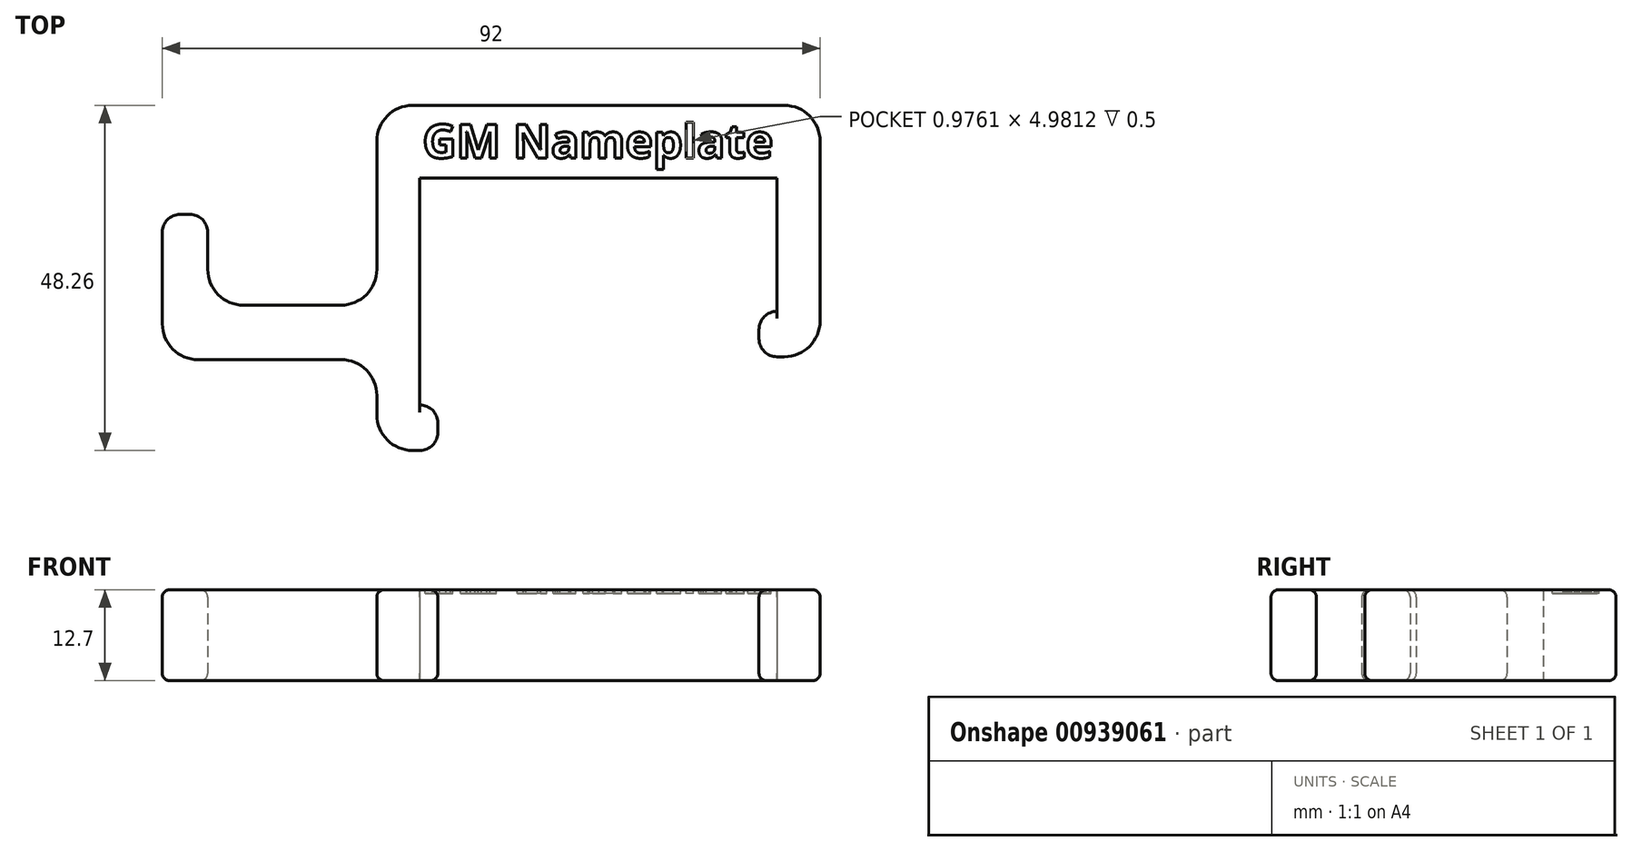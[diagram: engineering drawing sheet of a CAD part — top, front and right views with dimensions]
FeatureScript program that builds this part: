
annotation { "Feature Type Name" : "Feature", "Feature Type Description" : "" }
export const myFeature = defineFeature(function(context is Context, id is Id, definition is map)
    precondition{}
    {
        {
            var Q0;
            Q0=qCreatedBy(makeId("Top.planeOp"),FACE);
            var sketch = newSketch(context, id + "F0", { "sketchPlane" : qUnion([Q0])});
            skLineSegment(sketch, "E0.bottom", {"start": v(-25, 0) * mm, "end": v(25, 0) * mm});
            skLineSegment(sketch, "E0.top", {"start": v(-25, -10.16) * mm, "end": v(25, -10.16) * mm});
            skLineSegment(sketch, "E0.left", {"start": v(-25, 0) * mm, "end": v(-25, -10.16) * mm});
            skLineSegment(sketch, "E0.right", {"start": v(25, 0) * mm, "end": v(25, -10.16) * mm});
            skLineSegment(sketch, "E1.bottom", {"start": v(-25, 0) * mm, "end": v(-26, 0) * mm});
            skLineSegment(sketch, "E1.top", {"start": v(-25, -48.26) * mm, "end": v(-26, -48.26) * mm});
            skLineSegment(sketch, "E1.left", {"start": v(-25, 0) * mm, "end": v(-25, -48.26) * mm});
            skLineSegment(sketch, "E1.right", {"start": v(-31, -5) * mm, "end": v(-31, -22.94) * mm});
            skLineSegment(sketch, "E2.bottom", {"start": v(25, 0) * mm, "end": v(26, 0) * mm});
            skLineSegment(sketch, "E2.top", {"start": v(25, -35.16) * mm, "end": v(31, -35.16) * mm});
            skLineSegment(sketch, "E2.left", {"start": v(25, 0) * mm, "end": v(25, -35.16) * mm});
            skLineSegment(sketch, "E2.right", {"start": v(31, -5) * mm, "end": v(31, -35.16) * mm});
            skLineSegment(sketch, "E3.bottom", {"start": v(-36, -35.56) * mm, "end": v(-56, -35.56) * mm});
            skLineSegment(sketch, "E3.top", {"start": v(-36, -27.94) * mm, "end": v(-49.65, -27.94) * mm});
            skLineSegment(sketch, "E3.left", {"start": v(-31, -43.26) * mm, "end": v(-31, -40.56) * mm});
            skLineSegment(sketch, "E3.right", {"start": v(-61, -30.56) * mm, "end": v(-61, -27.94) * mm});
            skLineSegment(sketch, "E4.top", {"start": v(-61, -15.24) * mm, "end": v(-54.65, -15.24) * mm});
            skLineSegment(sketch, "E4.left", {"start": v(-61, -27.94) * mm, "end": v(-61, -15.24) * mm});
            skLineSegment(sketch, "E4.right", {"start": v(-54.65, -22.94) * mm, "end": v(-54.65, -15.24) * mm});
            skPoint(sketch, "E5.visualSharp", {"position": v(-31, 0) * mm});
            skArc(sketch, "E5.filletArc", {"start": v(-26, 0) * mm, "mid": v(-29.54, -1.46) * mm, "end": v(-31, -5) * mm});
            skPoint(sketch, "E6.visualSharp", {"position": v(31, 0) * mm});
            skArc(sketch, "E6.filletArc", {"start": v(31, -5) * mm, "mid": v(29.54, -1.46) * mm, "end": v(26, 0) * mm});
            skArc(sketch, "E7.filletArc", {"start": v(-36, -27.94) * mm, "mid": v(-32.46, -26.48) * mm, "end": v(-31, -22.94) * mm});
            skPoint(sketch, "E8.visualSharp", {"position": v(-31, -35.56) * mm});
            skArc(sketch, "E8.filletArc", {"start": v(-31, -40.56) * mm, "mid": v(-32.46, -37.02) * mm, "end": v(-36, -35.56) * mm});
            skArc(sketch, "E9.filletArc", {"start": v(-54.65, -22.94) * mm, "mid": v(-53.19, -26.48) * mm, "end": v(-49.65, -27.94) * mm});
            skLineSegment(sketch, "E10", {"start": v(-61, -27.94) * mm, "end": v(-49.65, -27.94) * mm, "construction": true});
            skPoint(sketch, "E11.visualSharp", {"position": v(-61, -35.56) * mm});
            skArc(sketch, "E11.filletArc", {"start": v(-61, -30.56) * mm, "mid": v(-59.54, -34.1) * mm, "end": v(-56, -35.56) * mm});
            skPoint(sketch, "E12.visualSharp", {"position": v(-31, -48.26) * mm});
            skArc(sketch, "E12.filletArc", {"start": v(-31, -43.26) * mm, "mid": v(-29.54, -46.8) * mm, "end": v(-26, -48.26) * mm});
            skLineSegment(sketch, "E13.bottom", {"start": v(25, -35.16) * mm, "end": v(22.46, -35.16) * mm});
            skLineSegment(sketch, "E13.top", {"start": v(25, -28.8) * mm, "end": v(22.46, -28.8) * mm});
            skLineSegment(sketch, "E13.left", {"start": v(25, -35.16) * mm, "end": v(25, -28.8) * mm});
            skLineSegment(sketch, "E13.right", {"start": v(22.46, -35.16) * mm, "end": v(22.46, -28.8) * mm});
            skLineSegment(sketch, "E14.bottom", {"start": v(-25, -48.26) * mm, "end": v(-22.46, -48.26) * mm});
            skLineSegment(sketch, "E14.top", {"start": v(-25, -41.91) * mm, "end": v(-22.46, -41.91) * mm});
            skLineSegment(sketch, "E14.left", {"start": v(-25, -48.26) * mm, "end": v(-25, -41.91) * mm});
            skLineSegment(sketch, "E14.right", {"start": v(-22.46, -48.26) * mm, "end": v(-22.46, -41.91) * mm});
            skSolve(sketch);
        }
        {
            var Q0;
            Q0 = qSketchRegion(id + "F0", true);
            extrude(context, id + "F1", {"entities" : qUnion([Q0]), "depth" : 12.7 * mm, "offsetDistance" : 25.4 * mm});
        }
        {
            var Q0;
            Q0=makeQuery(id+"F1.opExtrude","SWEPT_EDGE",EDGE,{"disambiguationData":[OSD([sQuery(id+"F0.wireOp",EDGE,"E4.top"),sQuery(id+"F0.wireOp",EDGE,"E4.left")])]});
            var Q1;
            Q1=makeQuery(id+"F1.opExtrude","SWEPT_EDGE",EDGE,{"disambiguationData":[OSD([sQuery(id+"F0.wireOp",EDGE,"E4.top"),sQuery(id+"F0.wireOp",EDGE,"E4.right")])]});
            fillet(context, id + "F2", {"entities" : qUnion([Q0, Q1]), "radius" : 2.5 * mm, "tangentPropagation" : true, "allowEdgeOverflow" : false});
        }
        {
            var Q0;
            Q0=makeQuery(id+"F1.opExtrude","SWEPT_EDGE",EDGE,{"disambiguationData":[OSD([sQuery(id+"F0.wireOp",EDGE,"E2.top"),sQuery(id+"F0.wireOp",EDGE,"E2.right")])]});
            fillet(context, id + "F3", {"entities" : qUnion([Q0]), "radius" : 5 * mm, "tangentPropagation" : true, "allowEdgeOverflow" : false});
        }
        {
            var Q0;
            Q0=makeQuery(id+"F1.opExtrude","SWEPT_EDGE",EDGE,{"disambiguationData":[OSD([sQuery(id+"F0.wireOp",EDGE,"E13.top"),sQuery(id+"F0.wireOp",EDGE,"E13.right")])]});
            fillet(context, id + "F4", {"entities" : qUnion([Q0]), "radius" : 2.54 * mm, "tangentPropagation" : true, "allowEdgeOverflow" : false});
        }
        {
            var Q0;
            Q0=makeQuery(id+"F1.opExtrude","SWEPT_EDGE",EDGE,{"disambiguationData":[OSD([sQuery(id+"F0.wireOp",EDGE,"E13.bottom"),sQuery(id+"F0.wireOp",EDGE,"E13.right")])]});
            fillet(context, id + "F5", {"entities" : qUnion([Q0]), "radius" : 2.54 * mm, "tangentPropagation" : true, "allowEdgeOverflow" : false});
        }
        {
            var Q0;
            Q0=makeQuery(id+"F1.opExtrude","CAP_FACE",FACE,{"disambiguationData":[OSD([sQuery(id+"F0.wireOp",EDGE,"E0.bottom"),sQuery(id+"F0.wireOp",EDGE,"E0.top"),sQuery(id+"F0.wireOp",EDGE,"E1.bottom"),sQuery(id+"F0.wireOp",EDGE,"E1.top"),sQuery(id+"F0.wireOp",EDGE,"E1.left"),sQuery(id+"F0.wireOp",EDGE,"E1.right"),sQuery(id+"F0.wireOp",EDGE,"E2.bottom"),sQuery(id+"F0.wireOp",EDGE,"E2.top"),sQuery(id+"F0.wireOp",EDGE,"E2.left"),sQuery(id+"F0.wireOp",EDGE,"E2.right"),sQuery(id+"F0.wireOp",EDGE,"E3.bottom"),sQuery(id+"F0.wireOp",EDGE,"E3.top"),sQuery(id+"F0.wireOp",EDGE,"E3.left"),sQuery(id+"F0.wireOp",EDGE,"E3.right"),sQuery(id+"F0.wireOp",EDGE,"E4.top"),sQuery(id+"F0.wireOp",EDGE,"E4.left"),sQuery(id+"F0.wireOp",EDGE,"E4.right"),sQuery(id+"F0.wireOp",EDGE,"E5.filletArc"),sQuery(id+"F0.wireOp",EDGE,"E6.filletArc"),sQuery(id+"F0.wireOp",EDGE,"E7.filletArc"),sQuery(id+"F0.wireOp",EDGE,"E8.filletArc"),sQuery(id+"F0.wireOp",EDGE,"E9.filletArc"),sQuery(id+"F0.wireOp",EDGE,"E11.filletArc"),sQuery(id+"F0.wireOp",EDGE,"E12.filletArc"),sQuery(id+"F0.wireOp",EDGE,"E13.bottom"),sQuery(id+"F0.wireOp",EDGE,"E13.top"),sQuery(id+"F0.wireOp",EDGE,"E13.right")])],"isStart":false});
            var sketch = newSketch(context, id + "F6", { "sketchPlane" : qUnion([Q0])});
            skText(sketch, "E15", { "text": "GM Nameplate", "fontName": "OpenSans-Bold.ttf"});
            const initialGuessF6  = {"E15": [-0.0246, -0.00735, 1, 0, 0.00472]};
            skSetInitialGuess(sketch, initialGuessF6);
            skSolve(sketch);
        }
        {
            var Q0;
            Q0 = qSketchRegion(id + "F6", true);
            extrude(context, id + "F7", {"entities" : qUnion([Q0]), "operationType" : NewBodyOperationType.REMOVE, "oppositeDirection" : true, "depth" : 0.5 * mm, "offsetDistance" : 25 * mm});
        }
        {
            var Q0;
            Q0=makeQuery(id+"F1.opExtrude","SWEPT_EDGE",EDGE,{"disambiguationData":[OSD([sQuery(id+"F0.wireOp",EDGE,"E14.top"),sQuery(id+"F0.wireOp",EDGE,"E14.right")])]});
            var Q1;
            Q1=makeQuery(id+"F1.opExtrude","SWEPT_EDGE",EDGE,{"disambiguationData":[OSD([sQuery(id+"F0.wireOp",EDGE,"E14.bottom"),sQuery(id+"F0.wireOp",EDGE,"E14.right")])]});
            fillet(context, id + "F8", {"entities" : qUnion([Q0, Q1]), "radius" : 2.5 * mm, "tangentPropagation" : true, "allowEdgeOverflow" : false});
        }
        {
            var Q0;
            Q0=makeQuery(id+"F1.opExtrude","CAP_EDGE",EDGE,{"disambiguationData":[OSD([sQuery(id+"F0.wireOp",EDGE,"E3.top")])],"isStart":true});
            var Q1;
            Q1=makeQuery(id+"F1.opExtrude","CAP_EDGE",EDGE,{"disambiguationData":[OSD([sQuery(id+"F0.wireOp",EDGE,"E9.filletArc")])],"isStart":true});
            var Q2;
            Q2=makeQuery(id+"F1.opExtrude","CAP_EDGE",EDGE,{"disambiguationData":[OSD([sQuery(id+"F0.wireOp",EDGE,"E4.right")])],"isStart":true});
            var Q3;
            Q3=makeQuery(id+"F1.opExtrude","CAP_EDGE",EDGE,{"disambiguationData":[OSD([sQuery(id+"F0.wireOp",EDGE,"E3.top")])],"isStart":false});
            var Q4;
            Q4=makeQuery(id+"F1.opExtrude","CAP_EDGE",EDGE,{"disambiguationData":[OSD([sQuery(id+"F0.wireOp",EDGE,"E9.filletArc")])],"isStart":false});
            var Q5;
            Q5=makeQuery(id+"F1.opExtrude","CAP_EDGE",EDGE,{"disambiguationData":[OSD([sQuery(id+"F0.wireOp",EDGE,"E4.right")])],"isStart":false});
            var Q6;
            {var subQ0=sQuery(id+"F0.wireOp",EDGE,"E4.right");var subQ1=sQuery(id+"F0.wireOp",EDGE,"E4.top");Q6=makeQuery(id+"F2.opFillet","BLEND_EDGE",EDGE,{"blendedFrom":[makeQuery(id+"F1.opExtrude","SWEPT_EDGE",EDGE,{"disambiguationData":[OSD([subQ1,subQ0])]}),makeQuery(id+"F1.opExtrude","CAP_FACE",FACE,{"disambiguationData":[OSD([sQuery(id+"F0.wireOp",EDGE,"E0.bottom"),sQuery(id+"F0.wireOp",EDGE,"E0.top"),sQuery(id+"F0.wireOp",EDGE,"E1.bottom"),sQuery(id+"F0.wireOp",EDGE,"E1.top"),sQuery(id+"F0.wireOp",EDGE,"E1.left"),sQuery(id+"F0.wireOp",EDGE,"E1.right"),sQuery(id+"F0.wireOp",EDGE,"E2.bottom"),sQuery(id+"F0.wireOp",EDGE,"E2.top"),sQuery(id+"F0.wireOp",EDGE,"E2.left"),sQuery(id+"F0.wireOp",EDGE,"E2.right"),sQuery(id+"F0.wireOp",EDGE,"E3.bottom"),sQuery(id+"F0.wireOp",EDGE,"E3.top"),sQuery(id+"F0.wireOp",EDGE,"E3.left"),sQuery(id+"F0.wireOp",EDGE,"E3.right"),subQ1,sQuery(id+"F0.wireOp",EDGE,"E4.left"),subQ0,sQuery(id+"F0.wireOp",EDGE,"E5.filletArc"),sQuery(id+"F0.wireOp",EDGE,"E6.filletArc"),sQuery(id+"F0.wireOp",EDGE,"E7.filletArc"),sQuery(id+"F0.wireOp",EDGE,"E8.filletArc"),sQuery(id+"F0.wireOp",EDGE,"E9.filletArc"),sQuery(id+"F0.wireOp",EDGE,"E11.filletArc"),sQuery(id+"F0.wireOp",EDGE,"E12.filletArc"),sQuery(id+"F0.wireOp",EDGE,"E13.bottom"),sQuery(id+"F0.wireOp",EDGE,"E13.top"),sQuery(id+"F0.wireOp",EDGE,"E13.right"),sQuery(id+"F0.wireOp",EDGE,"E14.bottom"),sQuery(id+"F0.wireOp",EDGE,"E14.top"),sQuery(id+"F0.wireOp",EDGE,"E14.right")])],"isStart":true})],"blendedInto":[makeQuery(id+"F1.opExtrude","CAP_FACE",FACE,{"disambiguationData":[OSD([sQuery(id+"F0.wireOp",EDGE,"E0.bottom"),sQuery(id+"F0.wireOp",EDGE,"E0.top"),sQuery(id+"F0.wireOp",EDGE,"E1.bottom"),sQuery(id+"F0.wireOp",EDGE,"E1.top"),sQuery(id+"F0.wireOp",EDGE,"E1.left"),sQuery(id+"F0.wireOp",EDGE,"E1.right"),sQuery(id+"F0.wireOp",EDGE,"E2.bottom"),sQuery(id+"F0.wireOp",EDGE,"E2.top"),sQuery(id+"F0.wireOp",EDGE,"E2.left"),sQuery(id+"F0.wireOp",EDGE,"E2.right"),sQuery(id+"F0.wireOp",EDGE,"E3.bottom"),sQuery(id+"F0.wireOp",EDGE,"E3.top"),sQuery(id+"F0.wireOp",EDGE,"E3.left"),sQuery(id+"F0.wireOp",EDGE,"E3.right"),subQ1,sQuery(id+"F0.wireOp",EDGE,"E4.left"),subQ0,sQuery(id+"F0.wireOp",EDGE,"E5.filletArc"),sQuery(id+"F0.wireOp",EDGE,"E6.filletArc"),sQuery(id+"F0.wireOp",EDGE,"E7.filletArc"),sQuery(id+"F0.wireOp",EDGE,"E8.filletArc"),sQuery(id+"F0.wireOp",EDGE,"E9.filletArc"),sQuery(id+"F0.wireOp",EDGE,"E11.filletArc"),sQuery(id+"F0.wireOp",EDGE,"E12.filletArc"),sQuery(id+"F0.wireOp",EDGE,"E13.bottom"),sQuery(id+"F0.wireOp",EDGE,"E13.top"),sQuery(id+"F0.wireOp",EDGE,"E13.right"),sQuery(id+"F0.wireOp",EDGE,"E14.bottom"),sQuery(id+"F0.wireOp",EDGE,"E14.top"),sQuery(id+"F0.wireOp",EDGE,"E14.right")])],"isStart":true})]});}
            var Q7;
            Q7=makeQuery(id+"F1.opExtrude","CAP_EDGE",EDGE,{"disambiguationData":[OSD([sQuery(id+"F0.wireOp",EDGE,"E4.top")])],"isStart":true});
            var Q8;
            {var subQ0=sQuery(id+"F0.wireOp",EDGE,"E4.left");var subQ1=sQuery(id+"F0.wireOp",EDGE,"E4.top");Q8=makeQuery(id+"F2.opFillet","BLEND_EDGE",EDGE,{"blendedFrom":[makeQuery(id+"F1.opExtrude","SWEPT_EDGE",EDGE,{"disambiguationData":[OSD([subQ1,subQ0])]}),makeQuery(id+"F1.opExtrude","CAP_FACE",FACE,{"disambiguationData":[OSD([sQuery(id+"F0.wireOp",EDGE,"E0.bottom"),sQuery(id+"F0.wireOp",EDGE,"E0.top"),sQuery(id+"F0.wireOp",EDGE,"E1.bottom"),sQuery(id+"F0.wireOp",EDGE,"E1.top"),sQuery(id+"F0.wireOp",EDGE,"E1.left"),sQuery(id+"F0.wireOp",EDGE,"E1.right"),sQuery(id+"F0.wireOp",EDGE,"E2.bottom"),sQuery(id+"F0.wireOp",EDGE,"E2.top"),sQuery(id+"F0.wireOp",EDGE,"E2.left"),sQuery(id+"F0.wireOp",EDGE,"E2.right"),sQuery(id+"F0.wireOp",EDGE,"E3.bottom"),sQuery(id+"F0.wireOp",EDGE,"E3.top"),sQuery(id+"F0.wireOp",EDGE,"E3.left"),sQuery(id+"F0.wireOp",EDGE,"E3.right"),subQ1,subQ0,sQuery(id+"F0.wireOp",EDGE,"E4.right"),sQuery(id+"F0.wireOp",EDGE,"E5.filletArc"),sQuery(id+"F0.wireOp",EDGE,"E6.filletArc"),sQuery(id+"F0.wireOp",EDGE,"E7.filletArc"),sQuery(id+"F0.wireOp",EDGE,"E8.filletArc"),sQuery(id+"F0.wireOp",EDGE,"E9.filletArc"),sQuery(id+"F0.wireOp",EDGE,"E11.filletArc"),sQuery(id+"F0.wireOp",EDGE,"E12.filletArc"),sQuery(id+"F0.wireOp",EDGE,"E13.bottom"),sQuery(id+"F0.wireOp",EDGE,"E13.top"),sQuery(id+"F0.wireOp",EDGE,"E13.right"),sQuery(id+"F0.wireOp",EDGE,"E14.bottom"),sQuery(id+"F0.wireOp",EDGE,"E14.top"),sQuery(id+"F0.wireOp",EDGE,"E14.right")])],"isStart":true})],"blendedInto":[makeQuery(id+"F1.opExtrude","CAP_FACE",FACE,{"disambiguationData":[OSD([sQuery(id+"F0.wireOp",EDGE,"E0.bottom"),sQuery(id+"F0.wireOp",EDGE,"E0.top"),sQuery(id+"F0.wireOp",EDGE,"E1.bottom"),sQuery(id+"F0.wireOp",EDGE,"E1.top"),sQuery(id+"F0.wireOp",EDGE,"E1.left"),sQuery(id+"F0.wireOp",EDGE,"E1.right"),sQuery(id+"F0.wireOp",EDGE,"E2.bottom"),sQuery(id+"F0.wireOp",EDGE,"E2.top"),sQuery(id+"F0.wireOp",EDGE,"E2.left"),sQuery(id+"F0.wireOp",EDGE,"E2.right"),sQuery(id+"F0.wireOp",EDGE,"E3.bottom"),sQuery(id+"F0.wireOp",EDGE,"E3.top"),sQuery(id+"F0.wireOp",EDGE,"E3.left"),sQuery(id+"F0.wireOp",EDGE,"E3.right"),subQ1,subQ0,sQuery(id+"F0.wireOp",EDGE,"E4.right"),sQuery(id+"F0.wireOp",EDGE,"E5.filletArc"),sQuery(id+"F0.wireOp",EDGE,"E6.filletArc"),sQuery(id+"F0.wireOp",EDGE,"E7.filletArc"),sQuery(id+"F0.wireOp",EDGE,"E8.filletArc"),sQuery(id+"F0.wireOp",EDGE,"E9.filletArc"),sQuery(id+"F0.wireOp",EDGE,"E11.filletArc"),sQuery(id+"F0.wireOp",EDGE,"E12.filletArc"),sQuery(id+"F0.wireOp",EDGE,"E13.bottom"),sQuery(id+"F0.wireOp",EDGE,"E13.top"),sQuery(id+"F0.wireOp",EDGE,"E13.right"),sQuery(id+"F0.wireOp",EDGE,"E14.bottom"),sQuery(id+"F0.wireOp",EDGE,"E14.top"),sQuery(id+"F0.wireOp",EDGE,"E14.right")])],"isStart":true})]});}
            var Q9;
            {var subQ0=sQuery(id+"F0.wireOp",EDGE,"E4.left");var subQ1=sQuery(id+"F0.wireOp",EDGE,"E4.top");Q9=makeQuery(id+"F2.opFillet","BLEND_EDGE",EDGE,{"blendedFrom":[makeQuery(id+"F1.opExtrude","SWEPT_EDGE",EDGE,{"disambiguationData":[OSD([subQ1,subQ0])]}),makeQuery(id+"F1.opExtrude","CAP_FACE",FACE,{"disambiguationData":[OSD([sQuery(id+"F0.wireOp",EDGE,"E0.bottom"),sQuery(id+"F0.wireOp",EDGE,"E0.top"),sQuery(id+"F0.wireOp",EDGE,"E1.bottom"),sQuery(id+"F0.wireOp",EDGE,"E1.top"),sQuery(id+"F0.wireOp",EDGE,"E1.left"),sQuery(id+"F0.wireOp",EDGE,"E1.right"),sQuery(id+"F0.wireOp",EDGE,"E2.bottom"),sQuery(id+"F0.wireOp",EDGE,"E2.top"),sQuery(id+"F0.wireOp",EDGE,"E2.left"),sQuery(id+"F0.wireOp",EDGE,"E2.right"),sQuery(id+"F0.wireOp",EDGE,"E3.bottom"),sQuery(id+"F0.wireOp",EDGE,"E3.top"),sQuery(id+"F0.wireOp",EDGE,"E3.left"),sQuery(id+"F0.wireOp",EDGE,"E3.right"),subQ1,subQ0,sQuery(id+"F0.wireOp",EDGE,"E4.right"),sQuery(id+"F0.wireOp",EDGE,"E5.filletArc"),sQuery(id+"F0.wireOp",EDGE,"E6.filletArc"),sQuery(id+"F0.wireOp",EDGE,"E7.filletArc"),sQuery(id+"F0.wireOp",EDGE,"E8.filletArc"),sQuery(id+"F0.wireOp",EDGE,"E9.filletArc"),sQuery(id+"F0.wireOp",EDGE,"E11.filletArc"),sQuery(id+"F0.wireOp",EDGE,"E12.filletArc"),sQuery(id+"F0.wireOp",EDGE,"E13.bottom"),sQuery(id+"F0.wireOp",EDGE,"E13.top"),sQuery(id+"F0.wireOp",EDGE,"E13.right"),sQuery(id+"F0.wireOp",EDGE,"E14.bottom"),sQuery(id+"F0.wireOp",EDGE,"E14.top"),sQuery(id+"F0.wireOp",EDGE,"E14.right")])],"isStart":false})],"blendedInto":[makeQuery(id+"F1.opExtrude","CAP_FACE",FACE,{"disambiguationData":[OSD([sQuery(id+"F0.wireOp",EDGE,"E0.bottom"),sQuery(id+"F0.wireOp",EDGE,"E0.top"),sQuery(id+"F0.wireOp",EDGE,"E1.bottom"),sQuery(id+"F0.wireOp",EDGE,"E1.top"),sQuery(id+"F0.wireOp",EDGE,"E1.left"),sQuery(id+"F0.wireOp",EDGE,"E1.right"),sQuery(id+"F0.wireOp",EDGE,"E2.bottom"),sQuery(id+"F0.wireOp",EDGE,"E2.top"),sQuery(id+"F0.wireOp",EDGE,"E2.left"),sQuery(id+"F0.wireOp",EDGE,"E2.right"),sQuery(id+"F0.wireOp",EDGE,"E3.bottom"),sQuery(id+"F0.wireOp",EDGE,"E3.top"),sQuery(id+"F0.wireOp",EDGE,"E3.left"),sQuery(id+"F0.wireOp",EDGE,"E3.right"),subQ1,subQ0,sQuery(id+"F0.wireOp",EDGE,"E4.right"),sQuery(id+"F0.wireOp",EDGE,"E5.filletArc"),sQuery(id+"F0.wireOp",EDGE,"E6.filletArc"),sQuery(id+"F0.wireOp",EDGE,"E7.filletArc"),sQuery(id+"F0.wireOp",EDGE,"E8.filletArc"),sQuery(id+"F0.wireOp",EDGE,"E9.filletArc"),sQuery(id+"F0.wireOp",EDGE,"E11.filletArc"),sQuery(id+"F0.wireOp",EDGE,"E12.filletArc"),sQuery(id+"F0.wireOp",EDGE,"E13.bottom"),sQuery(id+"F0.wireOp",EDGE,"E13.top"),sQuery(id+"F0.wireOp",EDGE,"E13.right"),sQuery(id+"F0.wireOp",EDGE,"E14.bottom"),sQuery(id+"F0.wireOp",EDGE,"E14.top"),sQuery(id+"F0.wireOp",EDGE,"E14.right")])],"isStart":false})]});}
            var Q10;
            Q10=makeQuery(id+"F1.opExtrude","CAP_EDGE",EDGE,{"disambiguationData":[OSD([sQuery(id+"F0.wireOp",EDGE,"E4.top")])],"isStart":false});
            var Q11;
            {var subQ0=sQuery(id+"F0.wireOp",EDGE,"E4.right");var subQ1=sQuery(id+"F0.wireOp",EDGE,"E4.top");Q11=makeQuery(id+"F2.opFillet","BLEND_EDGE",EDGE,{"blendedFrom":[makeQuery(id+"F1.opExtrude","SWEPT_EDGE",EDGE,{"disambiguationData":[OSD([subQ1,subQ0])]}),makeQuery(id+"F1.opExtrude","CAP_FACE",FACE,{"disambiguationData":[OSD([sQuery(id+"F0.wireOp",EDGE,"E0.bottom"),sQuery(id+"F0.wireOp",EDGE,"E0.top"),sQuery(id+"F0.wireOp",EDGE,"E1.bottom"),sQuery(id+"F0.wireOp",EDGE,"E1.top"),sQuery(id+"F0.wireOp",EDGE,"E1.left"),sQuery(id+"F0.wireOp",EDGE,"E1.right"),sQuery(id+"F0.wireOp",EDGE,"E2.bottom"),sQuery(id+"F0.wireOp",EDGE,"E2.top"),sQuery(id+"F0.wireOp",EDGE,"E2.left"),sQuery(id+"F0.wireOp",EDGE,"E2.right"),sQuery(id+"F0.wireOp",EDGE,"E3.bottom"),sQuery(id+"F0.wireOp",EDGE,"E3.top"),sQuery(id+"F0.wireOp",EDGE,"E3.left"),sQuery(id+"F0.wireOp",EDGE,"E3.right"),subQ1,sQuery(id+"F0.wireOp",EDGE,"E4.left"),subQ0,sQuery(id+"F0.wireOp",EDGE,"E5.filletArc"),sQuery(id+"F0.wireOp",EDGE,"E6.filletArc"),sQuery(id+"F0.wireOp",EDGE,"E7.filletArc"),sQuery(id+"F0.wireOp",EDGE,"E8.filletArc"),sQuery(id+"F0.wireOp",EDGE,"E9.filletArc"),sQuery(id+"F0.wireOp",EDGE,"E11.filletArc"),sQuery(id+"F0.wireOp",EDGE,"E12.filletArc"),sQuery(id+"F0.wireOp",EDGE,"E13.bottom"),sQuery(id+"F0.wireOp",EDGE,"E13.top"),sQuery(id+"F0.wireOp",EDGE,"E13.right"),sQuery(id+"F0.wireOp",EDGE,"E14.bottom"),sQuery(id+"F0.wireOp",EDGE,"E14.top"),sQuery(id+"F0.wireOp",EDGE,"E14.right")])],"isStart":false})],"blendedInto":[makeQuery(id+"F1.opExtrude","CAP_FACE",FACE,{"disambiguationData":[OSD([sQuery(id+"F0.wireOp",EDGE,"E0.bottom"),sQuery(id+"F0.wireOp",EDGE,"E0.top"),sQuery(id+"F0.wireOp",EDGE,"E1.bottom"),sQuery(id+"F0.wireOp",EDGE,"E1.top"),sQuery(id+"F0.wireOp",EDGE,"E1.left"),sQuery(id+"F0.wireOp",EDGE,"E1.right"),sQuery(id+"F0.wireOp",EDGE,"E2.bottom"),sQuery(id+"F0.wireOp",EDGE,"E2.top"),sQuery(id+"F0.wireOp",EDGE,"E2.left"),sQuery(id+"F0.wireOp",EDGE,"E2.right"),sQuery(id+"F0.wireOp",EDGE,"E3.bottom"),sQuery(id+"F0.wireOp",EDGE,"E3.top"),sQuery(id+"F0.wireOp",EDGE,"E3.left"),sQuery(id+"F0.wireOp",EDGE,"E3.right"),subQ1,sQuery(id+"F0.wireOp",EDGE,"E4.left"),subQ0,sQuery(id+"F0.wireOp",EDGE,"E5.filletArc"),sQuery(id+"F0.wireOp",EDGE,"E6.filletArc"),sQuery(id+"F0.wireOp",EDGE,"E7.filletArc"),sQuery(id+"F0.wireOp",EDGE,"E8.filletArc"),sQuery(id+"F0.wireOp",EDGE,"E9.filletArc"),sQuery(id+"F0.wireOp",EDGE,"E11.filletArc"),sQuery(id+"F0.wireOp",EDGE,"E12.filletArc"),sQuery(id+"F0.wireOp",EDGE,"E13.bottom"),sQuery(id+"F0.wireOp",EDGE,"E13.top"),sQuery(id+"F0.wireOp",EDGE,"E13.right"),sQuery(id+"F0.wireOp",EDGE,"E14.bottom"),sQuery(id+"F0.wireOp",EDGE,"E14.top"),sQuery(id+"F0.wireOp",EDGE,"E14.right")])],"isStart":false})]});}
            fillet(context, id + "F9", {"entities" : qUnion([Q0, Q1, Q2, Q3, Q4, Q5, Q6, Q7, Q8, Q9, Q10, Q11]), "radius" : 1 * mm, "tangentPropagation" : true, "allowEdgeOverflow" : false});
        }
    });
